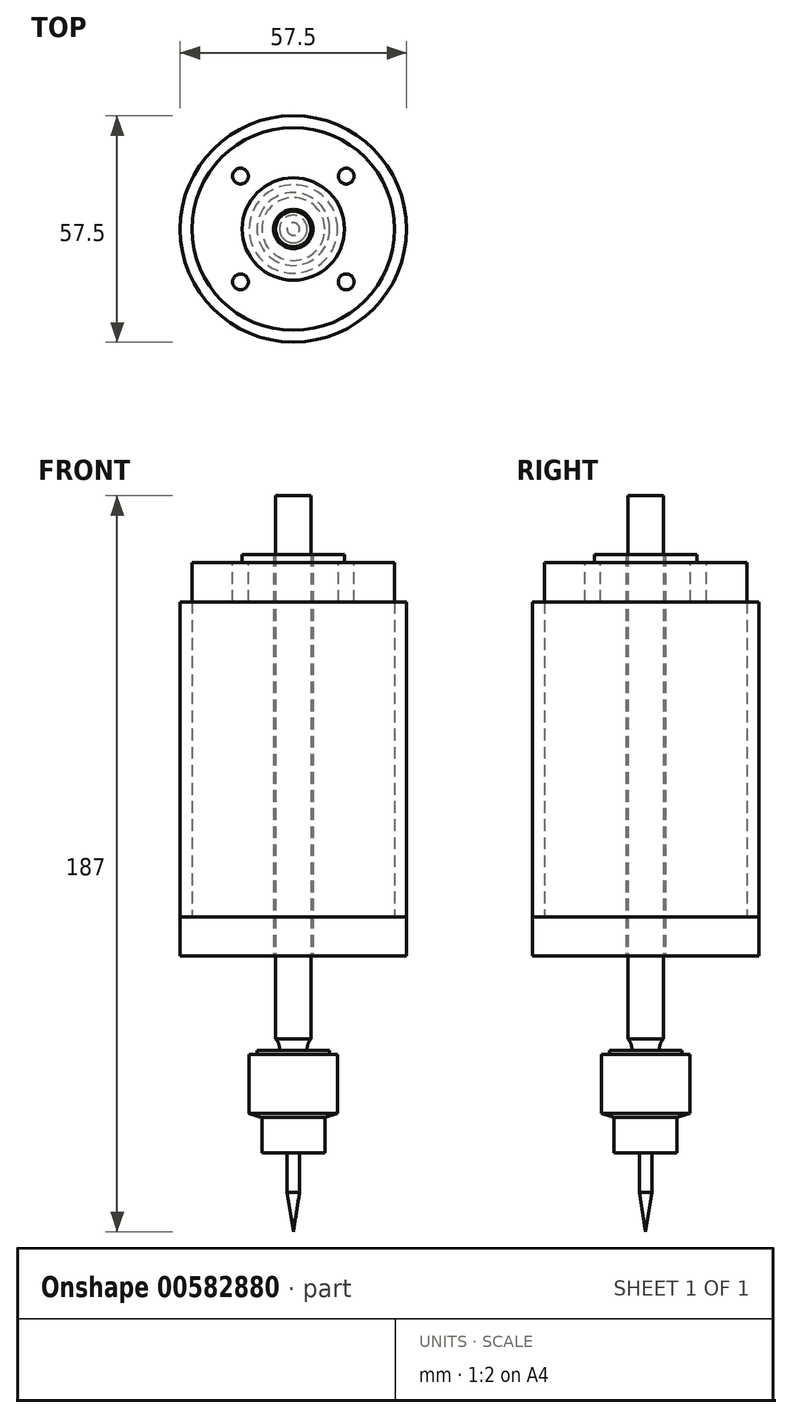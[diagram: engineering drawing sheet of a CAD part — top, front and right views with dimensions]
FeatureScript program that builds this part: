
annotation { "Feature Type Name" : "Feature", "Feature Type Description" : "" }
export const myFeature = defineFeature(function(context is Context, id is Id, definition is map)
    precondition{}
    {
        {
            var Q0;
            Q0=qCreatedBy(makeId("Front.planeOp"),FACE);
            var sketch = newSketch(context, id + "F0", { "sketchPlane" : qUnion([Q0])});
            skLineSegment(sketch, "E0", {"start": v(0, 117) * mm, "end": v(4.5, 117) * mm});
            skLineSegment(sketch, "E1", {"start": v(4.5, 117) * mm, "end": v(4.5, -21) * mm});
            skLineSegment(sketch, "E2", {"start": v(4.5, -21) * mm, "end": v(3.5, -21) * mm});
            skLineSegment(sketch, "E3", {"start": v(3.5, -21) * mm, "end": v(3.5, -24) * mm});
            skLineSegment(sketch, "E4", {"start": v(3.5, -24) * mm, "end": v(9.25, -24) * mm});
            skLineSegment(sketch, "E5", {"start": v(9.25, -24) * mm, "end": v(9.25, -25) * mm});
            skLineSegment(sketch, "E6", {"start": v(9.25, -25) * mm, "end": v(11.25, -25) * mm});
            skLineSegment(sketch, "E7", {"start": v(11.25, -25) * mm, "end": v(11.25, -40) * mm});
            skLineSegment(sketch, "E8", {"start": v(11.25, -40) * mm, "end": v(8, -41) * mm});
            skLineSegment(sketch, "E9", {"start": v(8, -41) * mm, "end": v(8, -50) * mm});
            skLineSegment(sketch, "E10", {"start": v(8, -50) * mm, "end": v(0, -50) * mm});
            skLineSegment(sketch, "E11", {"start": v(0, -50) * mm, "end": v(0, 117) * mm});
            skLineSegment(sketch, "E12.bottom", {"start": v(-13, 100) * mm, "end": v(-25.75, 100) * mm});
            skLineSegment(sketch, "E12.top", {"start": v(0, 0) * mm, "end": v(-25.75, 0) * mm});
            skLineSegment(sketch, "E12.left", {"start": v(0, 100) * mm, "end": v(0, 0) * mm});
            skLineSegment(sketch, "E12.right", {"start": v(-25.75, 100) * mm, "end": v(-25.75, 10) * mm});
            skLineSegment(sketch, "E13", {"start": v(0, -50) * mm, "end": v(0, -70) * mm});
            skLineSegment(sketch, "E14", {"start": v(0, -70) * mm, "end": v(1.59, -60) * mm});
            skLineSegment(sketch, "E15", {"start": v(1.59, -60) * mm, "end": v(1.59, -50) * mm});
            skLineSegment(sketch, "E16", {"start": v(-13, 100) * mm, "end": v(-13, 102) * mm});
            skLineSegment(sketch, "E17", {"start": v(-13, 102) * mm, "end": v(0, 102) * mm});
            skLineSegment(sketch, "E18", {"start": v(-25.75, 90) * mm, "end": v(-28.75, 90) * mm});
            skLineSegment(sketch, "E19", {"start": v(-28.75, 90) * mm, "end": v(-28.75, 10) * mm});
            skLineSegment(sketch, "E20", {"start": v(-28.75, 10) * mm, "end": v(-25.75, 10) * mm});
            skLineSegment(sketch, "E21", {"start": v(-25.75, 0) * mm, "end": v(-28.75, 0) * mm});
            skLineSegment(sketch, "E22", {"start": v(-28.75, 0) * mm, "end": v(-28.75, 10) * mm});
            skSolve(sketch);
        }
        {
            var Q0;
            Q0=makeQuery(id+"F0.imprint","IMPRINT",FACE,{"disambiguationData":[TD([[makeQuery(id+"F0.imprint","IMPRINT",EDGE,{"derivedFrom":sQuery(id+"F0.wireOp",EDGE,"E12.bottom")}),1.0]])]});
            var Q1;
            Q1=sQuery(id+"F0.wireOp",EDGE,"E11");
            revolve(context, id + "F1", {"entities" : qUnion([Q0]), "axis" : qUnion([Q1]), "revolveType" : RevolveType.FULL});
        }
        {
            var Q0;
            {var subQ1=sQuery(id+"F0.wireOp",EDGE,"E0");Q0=makeQuery(id+"F0.imprint","IMPRINT",FACE,{"disambiguationData":[TD([[makeQuery(id+"F0.imprint","IMPRINT",EDGE,{"derivedFrom":subQ1}),-1.0]])]});}
            var Q1;
            {var subQ0=sQuery(id+"F0.wireOp",EDGE,"E13");Q1=makeQuery(id+"F0.imprint","IMPRINT",FACE,{"disambiguationData":[TD([[makeQuery(id+"F0.imprint","IMPRINT",EDGE,{"derivedFrom":subQ0}),1.0]])]});}
            var Q2;
            Q2=sQuery(id+"F0.wireOp",EDGE,"E11");
            revolve(context, id + "F2", {"entities" : qUnion([Q0, Q1]), "axis" : qUnion([Q2]), "revolveType" : RevolveType.FULL});
        }
        {
            var Q0;
            {var subQ2=sQuery(id+"F0.wireOp",EDGE,"E18");Q0=makeQuery(id+"F0.imprint","IMPRINT",FACE,{"disambiguationData":[TD([[makeQuery(id+"F0.imprint","IMPRINT",EDGE,{"derivedFrom":subQ2}),1.0]])]});}
            var Q1;
            Q1=sQuery(id+"F0.wireOp",EDGE,"E11");
            revolve(context, id + "F3", {"entities" : qUnion([Q0]), "axis" : qUnion([Q1]), "revolveType" : RevolveType.FULL});
        }
        {
            var Q0;
            Q0=makeQuery(id+"F2.opRevolve","SWEPT_BODY",BODY,{"disambiguationData":[OSD([sQuery(id+"F0.wireOp",EDGE,"E0"),sQuery(id+"F0.wireOp",EDGE,"E1"),sQuery(id+"F0.wireOp",EDGE,"E2"),sQuery(id+"F0.wireOp",EDGE,"E3"),sQuery(id+"F0.wireOp",EDGE,"E4"),sQuery(id+"F0.wireOp",EDGE,"E5"),sQuery(id+"F0.wireOp",EDGE,"E6"),sQuery(id+"F0.wireOp",EDGE,"E7"),sQuery(id+"F0.wireOp",EDGE,"E8"),sQuery(id+"F0.wireOp",EDGE,"E9"),sQuery(id+"F0.wireOp",EDGE,"E10"),sQuery(id+"F0.wireOp",EDGE,"E11"),sQuery(id+"F0.wireOp",EDGE,"E12.left"),sQuery(id+"F0.wireOp",EDGE,"E13"),sQuery(id+"F0.wireOp",EDGE,"E14"),sQuery(id+"F0.wireOp",EDGE,"E15")])]});
            var Q1;
            Q1=makeQuery(id+"F1.opRevolve","SWEPT_BODY",BODY,{"disambiguationData":[OSD([sQuery(id+"F0.wireOp",EDGE,"E11"),sQuery(id+"F0.wireOp",EDGE,"E12.bottom"),sQuery(id+"F0.wireOp",EDGE,"E12.top"),sQuery(id+"F0.wireOp",EDGE,"E12.left"),sQuery(id+"F0.wireOp",EDGE,"E12.right"),sQuery(id+"F0.wireOp",EDGE,"E16"),sQuery(id+"F0.wireOp",EDGE,"E17"),sQuery(id+"F0.wireOp",EDGE,"E20"),sQuery(id+"F0.wireOp",EDGE,"E21"),sQuery(id+"F0.wireOp",EDGE,"E22")])]});
            booleanBodies(context, id + "F4", {"operationType" : BooleanOperationType.SUBTRACTION, "tools" : qUnion([Q0]), "targets" : qUnion([Q1]), "offset" : true, "offsetAll" : true, "offsetDistance" : 0.5 * mm, "keepTools" : true});
        }
        {
            var Q0;
            Q0=makeQuery(id+"F2.opRevolve","SWEPT_EDGE",EDGE,{"disambiguationData":[OSD([sQuery(id+"F0.wireOp",EDGE,"E2"),sQuery(id+"F0.wireOp",EDGE,"E3")])]});
            fillet(context, id + "F5", {"entities" : qUnion([Q0]), "radius" : 4 * mm, "tangentPropagation" : true, "allowEdgeOverflow" : false});
        }
        {
            var Q0;
            Q0=makeQuery(id+"F1.opRevolve","SWEPT_FACE",FACE,{"disambiguationData":[OSD([sQuery(id+"F0.wireOp",EDGE,"E12.bottom")])]});
            var sketch = newSketch(context, id + "F6", { "sketchPlane" : qUnion([Q0])});
            skCircle(sketch, "E23", {"center": v(13.44, 13.44) * mm, "radius": 2 * mm});
            skLineSegment(sketch, "E24", {"start": v(13.44, 13.44) * mm, "end": v(0, 0) * mm, "construction": true});
            skCircle(sketch, "E25.1.0", {"center": v(-13.44, 13.44) * mm, "radius": 2 * mm});
            skCircle(sketch, "E25.2.0", {"center": v(-13.44, -13.44) * mm, "radius": 2 * mm});
            skCircle(sketch, "E25.3.0", {"center": v(13.44, -13.44) * mm, "radius": 2 * mm});
            skPoint(sketch, "E25.center", {"position": v(0, 0) * mm});
            skSolve(sketch);
        }
        {
            var Q0;
            Q0=makeQuery(id+"F6.imprint","IMPRINT",FACE,{"disambiguationData":[TD([[makeQuery(id+"F6.imprint","IMPRINT",EDGE,{"derivedFrom":sQuery(id+"F6.wireOp",EDGE,"E25.1.0")}),1.0]])]});
            var Q1;
            Q1=makeQuery(id+"F6.imprint","IMPRINT",FACE,{"disambiguationData":[TD([[makeQuery(id+"F6.imprint","IMPRINT",EDGE,{"derivedFrom":sQuery(id+"F6.wireOp",EDGE,"E23")}),1.0]])]});
            var Q2;
            Q2=makeQuery(id+"F6.imprint","IMPRINT",FACE,{"disambiguationData":[TD([[makeQuery(id+"F6.imprint","IMPRINT",EDGE,{"derivedFrom":sQuery(id+"F6.wireOp",EDGE,"E25.3.0")}),1.0]])]});
            var Q3;
            Q3=makeQuery(id+"F6.imprint","IMPRINT",FACE,{"disambiguationData":[TD([[makeQuery(id+"F6.imprint","IMPRINT",EDGE,{"derivedFrom":sQuery(id+"F6.wireOp",EDGE,"E25.2.0")}),1.0]])]});
            extrude(context, id + "F7", {"entities" : qUnion([Q0, Q1, Q2, Q3]), "operationType" : NewBodyOperationType.REMOVE, "oppositeDirection" : true, "depth" : 10 * mm, "offsetDistance" : 25 * mm});
        }
    });
